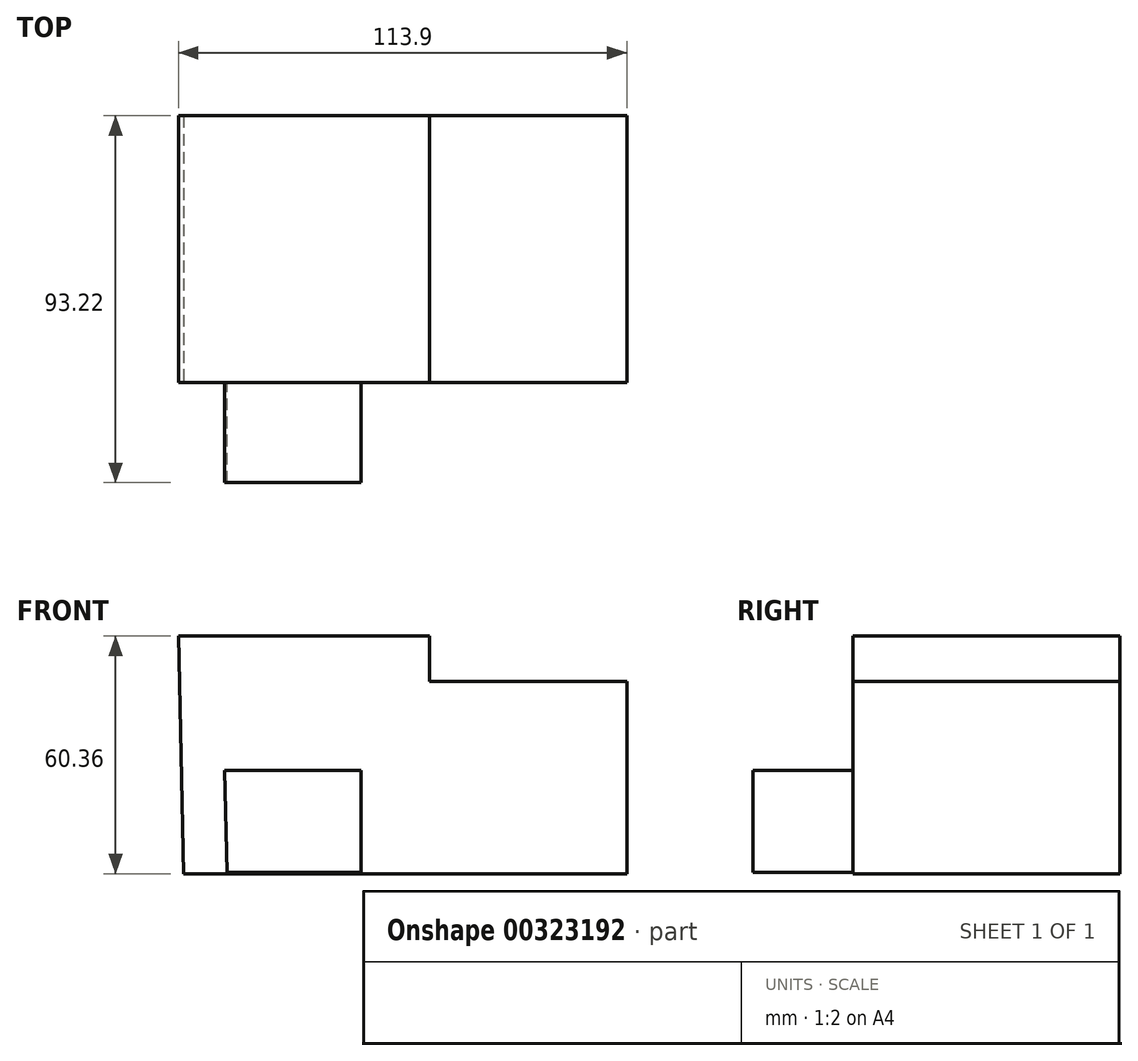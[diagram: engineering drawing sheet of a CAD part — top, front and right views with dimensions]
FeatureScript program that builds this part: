
annotation { "Feature Type Name" : "Feature", "Feature Type Description" : "" }
export const myFeature = defineFeature(function(context is Context, id is Id, definition is map)
    precondition{}
    {
        {
            var Q0;
            Q0=qCreatedBy(makeId("Front.planeOp"),FACE);
            var sketch = newSketch(context, id + "F0", { "sketchPlane" : qUnion([Q0])});
            skLineSegment(sketch, "E0", {"start": v(-60.97, 42.56) * mm, "end": v(2.79, 42.56) * mm});
            skLineSegment(sketch, "E1", {"start": v(2.79, 42.56) * mm, "end": v(2.79, 31.1) * mm});
            skLineSegment(sketch, "E2", {"start": v(2.79, 31.1) * mm, "end": v(52.93, 31.1) * mm});
            skLineSegment(sketch, "E3", {"start": v(52.93, 31.1) * mm, "end": v(52.93, -17.8) * mm});
            skLineSegment(sketch, "E4", {"start": v(52.93, -17.8) * mm, "end": v(-9.9, -17.8) * mm});
            skLineSegment(sketch, "E5", {"start": v(-59.74, -17.8) * mm, "end": v(-60.97, 42.56) * mm});
            skLineSegment(sketch, "E6", {"start": v(-59.74, -17.8) * mm, "end": v(0, -17.8) * mm});
            skLineSegment(sketch, "E7", {"start": v(-50.14, -17.8) * mm, "end": v(-50.62, 5.68) * mm});
            skLineSegment(sketch, "E8", {"start": v(-50.62, 5.68) * mm, "end": v(-18.88, 5.68) * mm});
            skLineSegment(sketch, "E9", {"start": v(-18.88, 5.68) * mm, "end": v(-18.4, -17.8) * mm});
            skLineSegment(sketch, "E10", {"start": v(-18.4, -17.8) * mm, "end": v(-50.14, -17.8) * mm});
            skSolve(sketch);
        }
        {
            var Q0;
            Q0=makeQuery(id+"F0.imprint","IMPRINT",FACE,{"disambiguationData":[TD([[makeQuery(id+"F0.imprint","IMPRINT",EDGE,{"derivedFrom":sQuery(id+"F0.wireOp",EDGE,"E7")}),-1.0]])]});
            var Q1;
            Q1=makeQuery(id+"F0.imprint","IMPRINT",FACE,{"disambiguationData":[TD([[makeQuery(id+"F0.imprint","IMPRINT",EDGE,{"derivedFrom":sQuery(id+"F0.wireOp",EDGE,"E0")}),-1.0]])]});
            extrude(context, id + "F1", {"entities" : qUnion([Q0, Q1]), "oppositeDirection" : true, "depth" : 67.82 * mm});
        }
        {
            var Q0;
            Q0=qCreatedBy(makeId("Front.planeOp"),FACE);
            var sketch = newSketch(context, id + "F2", { "sketchPlane" : qUnion([Q0])});
            skLineSegment(sketch, "E11", {"start": v(-49.21, 8.51) * mm, "end": v(-14.55, 8.51) * mm});
            skLineSegment(sketch, "E12", {"start": v(-14.55, 8.51) * mm, "end": v(-14.55, -17.49) * mm});
            skLineSegment(sketch, "E13", {"start": v(-14.55, -17.49) * mm, "end": v(-48.6, -17.49) * mm});
            skLineSegment(sketch, "E14", {"start": v(-48.6, -17.49) * mm, "end": v(-49.21, 8.51) * mm});
            skSolve(sketch);
        }
        {
            var Q0;
            Q0=makeQuery(id+"F2.imprint","IMPRINT",FACE,{"disambiguationData":[TD([[makeQuery(id+"F2.imprint","IMPRINT",EDGE,{"derivedFrom":sQuery(id+"F2.wireOp",EDGE,"E11")}),-1.0]])]});
            extrude(context, id + "F3", {"entities" : qUnion([Q0]), "operationType" : NewBodyOperationType.ADD, "depth" : 25.4 * mm});
        }
        {
            var Q0;
            Q0=makeQuery(id+"F1.opExtrude","CAP_FACE",FACE,{"disambiguationData":[OSD([sQuery(id+"F0.wireOp",EDGE,"E0"),sQuery(id+"F0.wireOp",EDGE,"E1"),sQuery(id+"F0.wireOp",EDGE,"E2"),sQuery(id+"F0.wireOp",EDGE,"E3"),sQuery(id+"F0.wireOp",EDGE,"E4"),sQuery(id+"F0.wireOp",EDGE,"E5"),sQuery(id+"F0.wireOp",EDGE,"E6"),sQuery(id+"F0.wireOp",EDGE,"E10")])],"isStart":true});
            extrude(context, id + "F4", {"entities" : qUnion([Q0]), "operationType" : NewBodyOperationType.ADD, "oppositeDirection" : true, "depth" : 9.9 * mm});
        }
    });
